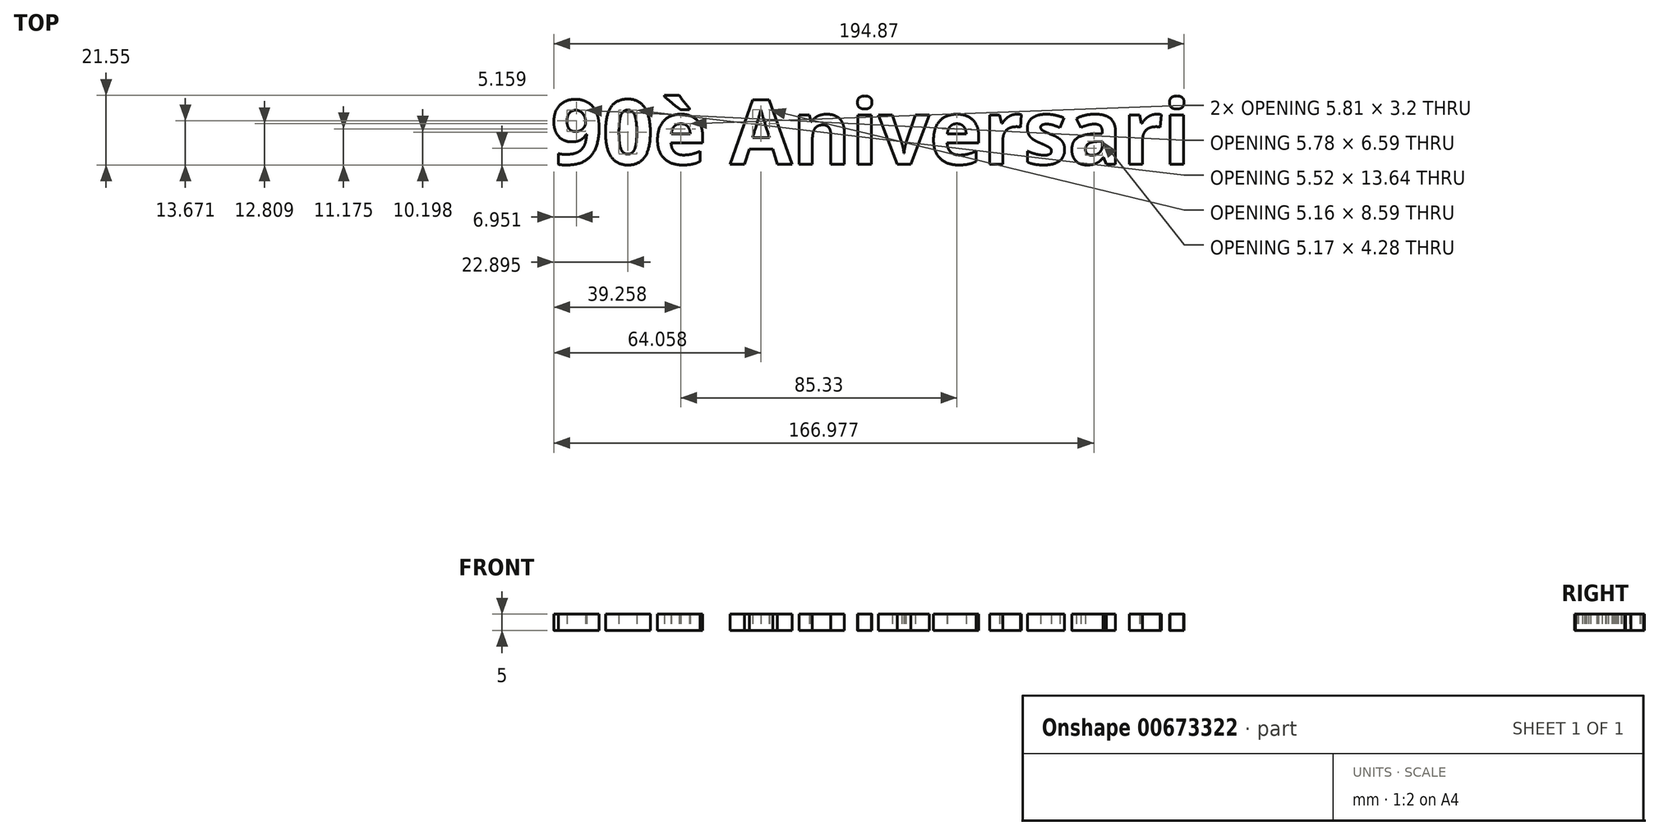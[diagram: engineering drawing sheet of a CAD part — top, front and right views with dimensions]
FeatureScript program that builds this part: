
annotation { "Feature Type Name" : "Feature", "Feature Type Description" : "" }
export const myFeature = defineFeature(function(context is Context, id is Id, definition is map)
    precondition{}
    {
        {
            var Q0;
            Q0=qCreatedBy(makeId("Top.planeOp"),FACE);
            var sketch = newSketch(context, id + "F0", { "sketchPlane" : qUnion([Q0])});
            skText(sketch, "E0", { "text": "90è Aniversari", "fontName": "OpenSans-Bold.ttf"});
            const initialGuessF0  = {"E0": [-0.02337, 0.01662, 1, 0, 0.02]};
            skSetInitialGuess(sketch, initialGuessF0);
            skSolve(sketch);
        }
        {
            var Q0;
            Q0 = qSketchRegion(id + "F0", true);
            extrude(context, id + "F1", {"entities" : qUnion([Q0]), "depth" : 5 * mm, "offsetDistance" : 25.4 * mm});
        }
    });
